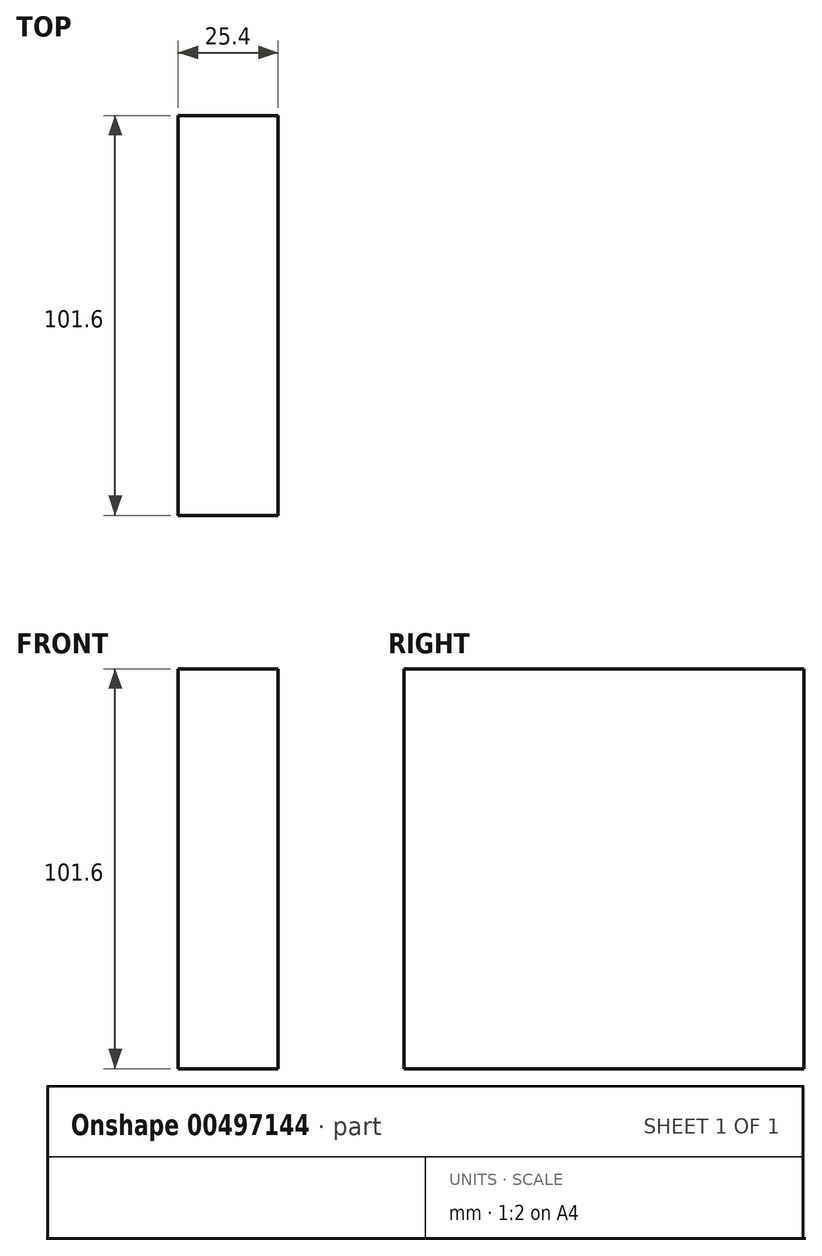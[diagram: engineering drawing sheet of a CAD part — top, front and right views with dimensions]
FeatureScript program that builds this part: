
annotation { "Feature Type Name" : "Feature", "Feature Type Description" : "" }
export const myFeature = defineFeature(function(context is Context, id is Id, definition is map)
    precondition{}
    {
        {
            var Q0;
            Q0=qCreatedBy(makeId("Right.planeOp"),FACE);
            var sketch = newSketch(context, id + "F0", { "sketchPlane" : qUnion([Q0])});
            skLineSegment(sketch, "E0.bottom", {"start": v(-46.3, 34.62) * mm, "end": v(55.3, 34.62) * mm});
            skLineSegment(sketch, "E0.top", {"start": v(-46.3, -66.98) * mm, "end": v(55.3, -66.98) * mm});
            skLineSegment(sketch, "E0.left", {"start": v(-46.3, 34.62) * mm, "end": v(-46.3, -66.98) * mm});
            skLineSegment(sketch, "E0.right", {"start": v(55.3, 34.62) * mm, "end": v(55.3, -66.98) * mm});
            skSolve(sketch);
        }
        {
            var Q0;
            Q0 = qSketchRegion(id + "F0", true);
            extrude(context, id + "F1", {"entities" : qUnion([Q0]), "depth" : 25.4 * mm, "offsetDistance" : 25.4 * mm});
        }
    });
